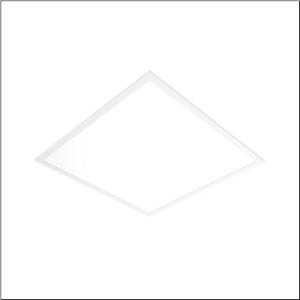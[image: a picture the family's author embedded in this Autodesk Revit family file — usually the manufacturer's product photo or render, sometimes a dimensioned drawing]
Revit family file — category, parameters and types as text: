
# Revit family: apollon_r__41_51mh12w72443m_8ad7
name_source: partatom
category: Lighting Fixtures
units: mm (PartAtom-declared; Revit-internal decimal feet)

## family parameters
Cut with Voids When Loaded = No
Host = Face
Light Source = No
Part Type = Normal
Room Calculation Point = No
Round Connector Dimension = Use Diameter
Shared = No

## types (1)
- Apollon® 41 (1 x LED, 3700 lm, 28.5 W, 4000K)
    Apparent Load = 29 VA
    CIE Flux Codes = 61 87 97 100 100
    Color Rendering = 80
    Color Temperature = 4000K
    Default Elevation = 1800 mm
    Description = Apollon® 41, office luminaire, primary optical cover: prismatic diffuser, of PS, light emission: direct distribution, primary light characteristic: symmetric, installation type: lay-in mounting, LED, rated luminous flux: 3.700lm, luminous efficacy: 130lm/W, light colour: 840, colour temperature: 4000K, with terminal, 3-pole, mains connection: 220..240V, AC, 50/60Hz, housing, of aluminium section, traffic white (RAL 9016), module: M600, length: 600mm, width: 600mm, height: 28mm, housing upper side, of sheet steel, protection rating (complete): IP20, protection rating (lamp compartment, on room side): IP40, insulation class (complete): insulation class II (safety insulation), certification: CE, ENEC, permissible operating ambient temperature: -25..+40°C, packaging unit: set of 6
    Height = 0 mm  [stored 0 ft]
    Lamp = 1 x LED
    Lamp Light Flux = 3700 lm
    Lamp Power = 28.5 W
    Lamp count = 1
    Length = 600 mm
    Luminous efficacy = 130 lm/W
    Manufacturer = Siteco
    ModVariant = No
    Model = 51MH12W72443M
    Mounting Place = Ceiling
    Mounting Type = Recessed
    Number of Poles = 1
    OnlyDefault = Yes
    Power Factor = 1
    Product Name = Apollon® 41
    Product group = office luminaire | ceiling recessed
    ProductGroupID = 400
    Protection Class = Protection class II
    Protection Degree = IP 20
    RLX_Detail_Level = 1
    RLX_Emergency_Light_Flux = 0 lm
    RLX_Emergency_Type = 0
    RLX_Emergency_Type_DB = No
    RlxData = <blob elided: 12197 chars, md5=d614303e>
    Socket = socket
    Standby Power = 0 W
    System Light Flux = 3700 lm
    System Power = 29 W
    Type Comments = Product without accessories
    Type Image = l_1291024.jpg
    URL = http://relux.com
    VarID = ---
    Voltage = 0 V
    Weight = 0.00 kg
    Width = 600 mm

note: [stored X ft] marks values corroborated as IEEE doubles in the binary element streams (Revit-internal decimal feet)

## geometry (parser evidence)
native form markers: Sweep x9
no freeform markers — native parametric forms only
